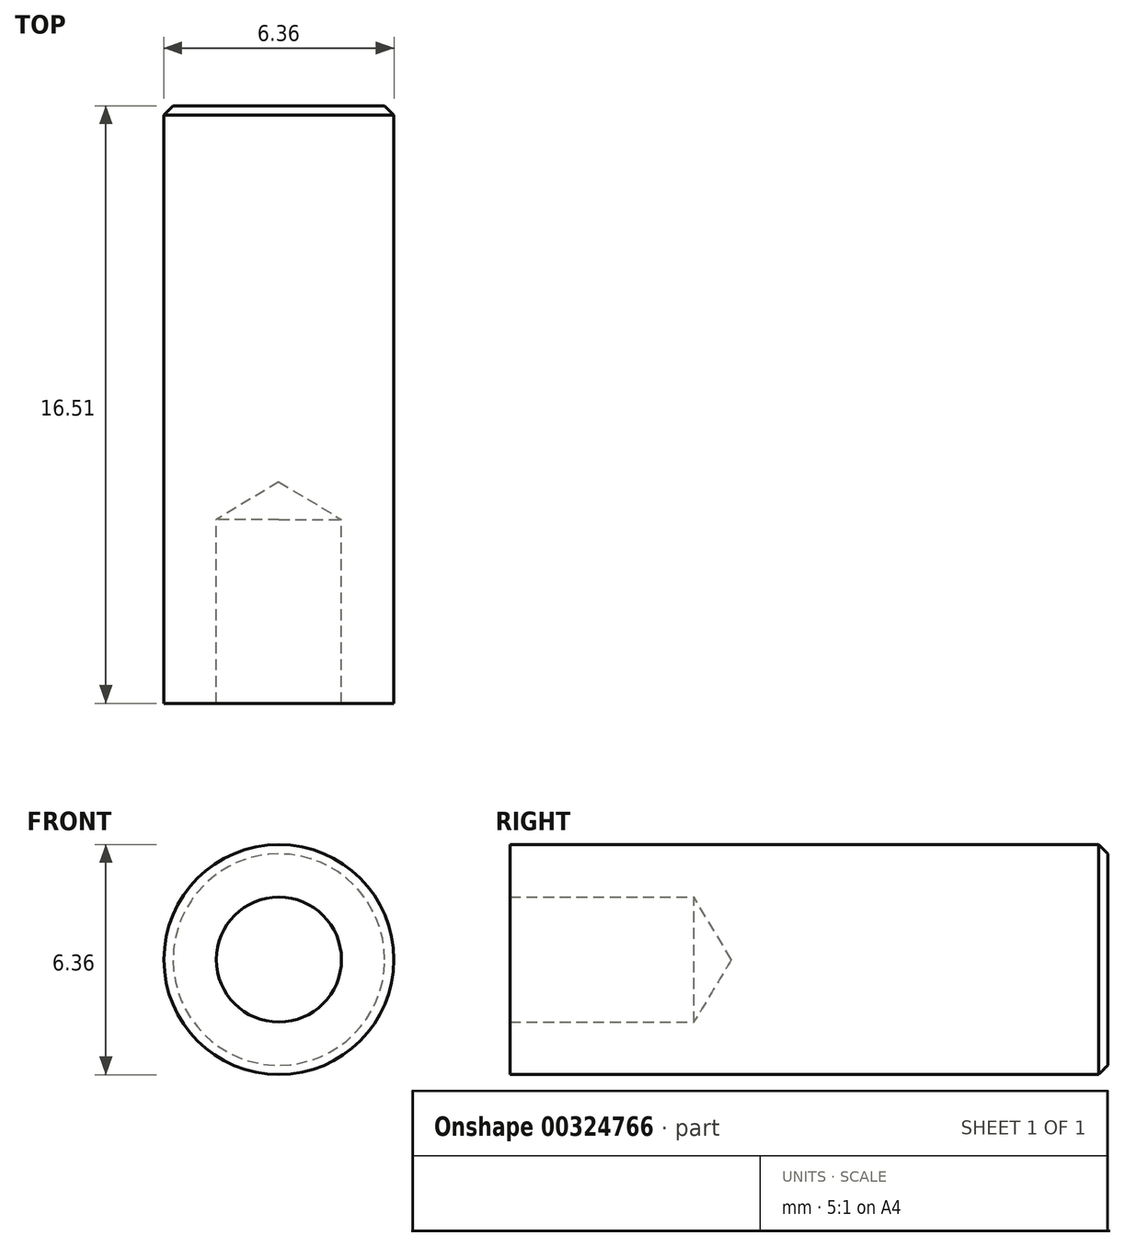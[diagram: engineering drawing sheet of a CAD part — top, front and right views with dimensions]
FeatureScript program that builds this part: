
annotation { "Feature Type Name" : "Feature", "Feature Type Description" : "" }
export const myFeature = defineFeature(function(context is Context, id is Id, definition is map)
    precondition{}
    {
        {
            var Q0;
            Q0=qCreatedBy(makeId("Front.planeOp"),FACE);
            var sketch = newSketch(context, id + "F0", { "sketchPlane" : qUnion([Q0])});
            skCircle(sketch, "E0", {"center": v(0, 0) * mm, "radius": 3.18 * mm});
            skSolve(sketch);
        }
        {
            var Q0;
            Q0=makeQuery(id+"F0.imprint","IMPRINT",FACE,{"disambiguationData":[TD([[makeQuery(id+"F0.imprint","IMPRINT",EDGE,{"derivedFrom":sQuery(id+"F0.wireOp",EDGE,"E0")}),1.0]])]});
            extrude(context, id + "F1", {"entities" : qUnion([Q0]), "depth" : 16.5 * mm, "offsetDistance" : 25.4 * mm});
        }
        {
            var Q0;
            Q0=makeQuery(id+"F1.opExtrude","CAP_FACE",FACE,{"disambiguationData":[OSD([sQuery(id+"F0.wireOp",EDGE,"E0")])],"isStart":false});
            var sketch = newSketch(context, id + "F2", { "sketchPlane" : qUnion([Q0])});
            skPoint(sketch, "E1", {"position": v(0, 0) * mm});
            skSolve(sketch);
        }
        {
            var Q0;
            Q0=sQuery(id+"F2.wireOp",VERTEX,"E1");
            var Q1;
            Q1=makeQuery(id+"F1.opExtrude","SWEPT_BODY",BODY,{"disambiguationData":[OSD([sQuery(id+"F0.wireOp",EDGE,"E0")])]});
            hole(context, id + "F3", {"style" : HoleStyle.SIMPLE, "endStyle" : HoleEndStyle.BLIND, "holeDiameter" : 3.45 * mm, "majorDiameter" : 6.35 * mm, "holeDepth" : 5.08 * mm, "tappedDepth" : 12.7 * mm, "tapClearance" : 3, "locations" : qUnion([Q0]), "scope" : qUnion([Q1])});
        }
        {
            var Q0;
            Q0=makeQuery(id+"F1.opExtrude","CAP_EDGE",EDGE,{"disambiguationData":[OSD([sQuery(id+"F0.wireOp",EDGE,"E0")])],"isStart":true});
            chamfer(context, id + "F4", {"entities" : qUnion([Q0]), "width" : 0.25 * mm, "tangentPropagation" : true});
        }
    });
